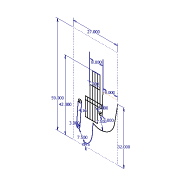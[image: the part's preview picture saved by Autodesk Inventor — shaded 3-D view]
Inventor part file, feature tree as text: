
AUTODESK INVENTOR PART (.ipt)
format: ipt  version: 2012 (Build 160160000, 160)  size: 87,040 bytes
history: native  units: in
note: dims shown in document units (in); Inventor stores cm internally (conversion verified against a paired STEP export)
features: sketch x1
ambient origin geometry x8: Origin, YZ Plane, XZ Plane, XY Plane, X Axis, Y Axis, Z Axis, Center Point
feature tree (1):
  sketch  "Sketch1"  dims[d36=27.0in d37=59.0in d38=2.0in d39=0.375in d40=7.5in d41=3.0in d42=32.0in d43=7.5in d44=9.0in d45=1.5in d46=0.0286in d47=2.0in d48=8.0in d49=42.0in]
